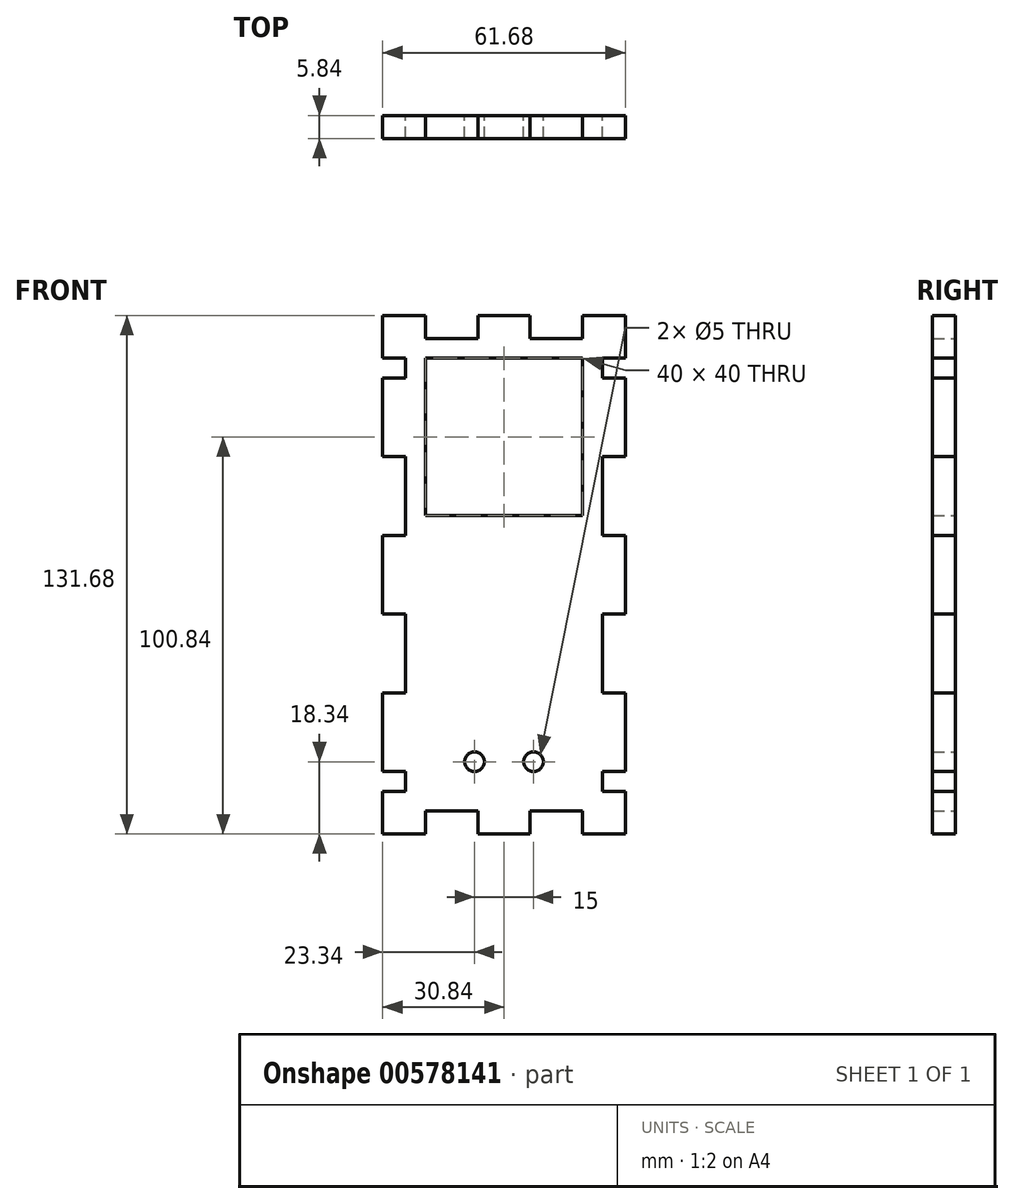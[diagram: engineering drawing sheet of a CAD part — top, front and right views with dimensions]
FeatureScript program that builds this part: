
annotation { "Feature Type Name" : "Feature", "Feature Type Description" : "" }
export const myFeature = defineFeature(function(context is Context, id is Id, definition is map)
    precondition{}
    {
        {
            var Q0;
            Q0=qCreatedBy(makeId("Front.planeOp"),FACE);
            var sketch = newSketch(context, id + "F0", { "sketchPlane" : qUnion([Q0])});
            skLineSegment(sketch, "E0.bottom", {"start": v(-25, 60) * mm, "end": v(25, 60) * mm});
            skLineSegment(sketch, "E0.top", {"start": v(-25, -60) * mm, "end": v(25, -60) * mm});
            skLineSegment(sketch, "E0.left", {"start": v(-25, 60) * mm, "end": v(-25, -60) * mm});
            skLineSegment(sketch, "E0.right", {"start": v(25, 60) * mm, "end": v(25, -60) * mm});
            skLineSegment(sketch, "E1.bottom", {"start": v(30.84, 65.84) * mm, "end": v(20, 65.84) * mm});
            skLineSegment(sketch, "E1.top", {"start": v(30.84, -65.84) * mm, "end": v(20, -65.84) * mm});
            skLineSegment(sketch, "E1.left", {"start": v(30.84, 65.84) * mm, "end": v(30.84, 55) * mm});
            skLineSegment(sketch, "E1.right", {"start": v(-30.84, 65.84) * mm, "end": v(-30.84, 55) * mm});
            skPoint(sketch, "E1.middle", {"position": v(0, 0) * mm});
            skLineSegment(sketch, "E2.bottom", {"start": v(6.67, -65.84) * mm, "end": v(-6.67, -65.84) * mm});
            skLineSegment(sketch, "E2.left", {"start": v(6.67, -65.84) * mm, "end": v(6.67, -60) * mm});
            skLineSegment(sketch, "E2.right", {"start": v(-6.67, -65.84) * mm, "end": v(-6.67, -60) * mm});
            skPoint(sketch, "E2.middle", {"position": v(0, -60) * mm});
            skPoint(sketch, "E3.middle", {"position": v(-25, -60) * mm});
            skLineSegment(sketch, "E4.bottom", {"start": v(-6.67, 65.84) * mm, "end": v(6.67, 65.84) * mm});
            skLineSegment(sketch, "E4.left", {"start": v(-6.67, 65.84) * mm, "end": v(-6.67, 60) * mm});
            skLineSegment(sketch, "E4.right", {"start": v(6.67, 65.84) * mm, "end": v(6.67, 60) * mm});
            skPoint(sketch, "E4.middle", {"position": v(0, 60) * mm});
            skPoint(sketch, "E5.middle", {"position": v(-25, 60) * mm});
            skPoint(sketch, "E6.middle", {"position": v(25, 60) * mm});
            skLineSegment(sketch, "E7.bottom", {"start": v(-6.67, 60) * mm, "end": v(-20, 60) * mm});
            skLineSegment(sketch, "E7.left", {"start": v(-6.67, 60) * mm, "end": v(-6.67, 65.84) * mm});
            skLineSegment(sketch, "E7.right", {"start": v(-20, 60) * mm, "end": v(-20, 65.84) * mm});
            skLineSegment(sketch, "E8.bottom", {"start": v(6.67, 60) * mm, "end": v(20, 60) * mm});
            skLineSegment(sketch, "E8.left", {"start": v(6.67, 60) * mm, "end": v(6.67, 65.84) * mm});
            skLineSegment(sketch, "E8.right", {"start": v(20, 60) * mm, "end": v(20, 65.84) * mm});
            skLineSegment(sketch, "E9.bottom", {"start": v(-6.67, -60) * mm, "end": v(-20, -60) * mm});
            skLineSegment(sketch, "E9.left", {"start": v(-6.67, -60) * mm, "end": v(-6.67, -65.84) * mm});
            skLineSegment(sketch, "E9.right", {"start": v(-20, -60) * mm, "end": v(-20, -65.84) * mm});
            skLineSegment(sketch, "E10.bottom", {"start": v(6.67, -60) * mm, "end": v(20, -60) * mm});
            skLineSegment(sketch, "E10.left", {"start": v(6.67, -60) * mm, "end": v(6.67, -65.84) * mm});
            skLineSegment(sketch, "E10.right", {"start": v(20, -60) * mm, "end": v(20, -65.84) * mm});
            skLineSegment(sketch, "E11.trimOffspring", {"start": v(-20, 65.84) * mm, "end": v(-30.84, 65.84) * mm});
            skLineSegment(sketch, "E12.trimOffspring", {"start": v(6.67, 65.84) * mm, "end": v(-6.67, 65.84) * mm});
            skPoint(sketch, "E13.orphan", {"position": v(-6.67, 54.16) * mm});
            skPoint(sketch, "E14.orphan", {"position": v(6.67, 54.16) * mm});
            skPoint(sketch, "E15.orphan", {"position": v(-6.67, -54.16) * mm});
            skPoint(sketch, "E16.orphan", {"position": v(6.67, -54.16) * mm});
            skLineSegment(sketch, "E17.trimOffspring", {"start": v(-20, -65.84) * mm, "end": v(-30.84, -65.84) * mm});
            skLineSegment(sketch, "E18.bottom", {"start": v(-25, 10) * mm, "end": v(-30.84, 10) * mm});
            skLineSegment(sketch, "E18.top", {"start": v(-25, -10) * mm, "end": v(-30.84, -10) * mm});
            skLineSegment(sketch, "E18.left", {"start": v(-25, 10) * mm, "end": v(-25, -10) * mm});
            skPoint(sketch, "E18.middle", {"position": v(-30.84, 0) * mm});
            skLineSegment(sketch, "E19.bottom", {"start": v(-30.84, 10) * mm, "end": v(-25, 10) * mm});
            skLineSegment(sketch, "E19.top", {"start": v(-30.84, 30) * mm, "end": v(-25, 30) * mm});
            skLineSegment(sketch, "E19.right", {"start": v(-25, 10) * mm, "end": v(-25, 30) * mm});
            skPoint(sketch, "E19.middle", {"position": v(-30.84, 20) * mm});
            skLineSegment(sketch, "E20.bottom", {"start": v(-30.84, -10) * mm, "end": v(-25, -10) * mm});
            skLineSegment(sketch, "E20.top", {"start": v(-30.84, -30) * mm, "end": v(-25, -30) * mm});
            skLineSegment(sketch, "E20.right", {"start": v(-25, -10) * mm, "end": v(-25, -30) * mm});
            skPoint(sketch, "E20.middle", {"position": v(-30.84, -20) * mm});
            skLineSegment(sketch, "E21.top", {"start": v(-30.84, 50) * mm, "end": v(-25, 50) * mm});
            skLineSegment(sketch, "E21.right", {"start": v(-25, 30) * mm, "end": v(-25, 50) * mm});
            skPoint(sketch, "E21.middle", {"position": v(-30.84, 40) * mm});
            skPoint(sketch, "E22.cornerSnap0", {"position": v(-36.68, 20) * mm});
            skLineSegment(sketch, "E23.top", {"start": v(-30.84, -50) * mm, "end": v(-25, -50) * mm});
            skLineSegment(sketch, "E23.right", {"start": v(-25, -30) * mm, "end": v(-25, -50) * mm});
            skPoint(sketch, "E23.middle", {"position": v(-30.84, -40) * mm});
            skLineSegment(sketch, "E24.top", {"start": v(-101.7, -103.63) * mm, "end": v(-97.86, -103.63) * mm});
            skLineSegment(sketch, "E25.bottom", {"start": v(-25, 55) * mm, "end": v(-30.84, 55) * mm});
            skLineSegment(sketch, "E25.top", {"start": v(-25, 50) * mm, "end": v(-30.84, 50) * mm});
            skLineSegment(sketch, "E25.left", {"start": v(-25, 55) * mm, "end": v(-25, 50) * mm});
            skLineSegment(sketch, "E26.bottom", {"start": v(-25, -50) * mm, "end": v(-30.84, -50) * mm});
            skLineSegment(sketch, "E26.top", {"start": v(-25, -55) * mm, "end": v(-30.84, -55) * mm});
            skLineSegment(sketch, "E26.left", {"start": v(-25, -50) * mm, "end": v(-25, -55) * mm});
            skLineSegment(sketch, "E27.bottom", {"start": v(25, 10) * mm, "end": v(30.84, 10) * mm});
            skLineSegment(sketch, "E27.top", {"start": v(25, -10) * mm, "end": v(30.84, -10) * mm});
            skLineSegment(sketch, "E27.left", {"start": v(25, 10) * mm, "end": v(25, -10) * mm});
            skPoint(sketch, "E27.middle", {"position": v(30.84, 0) * mm});
            skLineSegment(sketch, "E28.bottom", {"start": v(30.84, 10) * mm, "end": v(25, 10) * mm});
            skLineSegment(sketch, "E28.top", {"start": v(30.84, 30) * mm, "end": v(25, 30) * mm});
            skLineSegment(sketch, "E28.right", {"start": v(25, 10) * mm, "end": v(25, 30) * mm});
            skPoint(sketch, "E28.middle", {"position": v(30.84, 20) * mm});
            skLineSegment(sketch, "E29.bottom", {"start": v(30.84, -10) * mm, "end": v(25, -10) * mm});
            skLineSegment(sketch, "E29.top", {"start": v(30.84, -30) * mm, "end": v(25, -30) * mm});
            skLineSegment(sketch, "E29.right", {"start": v(25, -10) * mm, "end": v(25, -30) * mm});
            skPoint(sketch, "E29.middle", {"position": v(30.84, -20) * mm});
            skLineSegment(sketch, "E30.top", {"start": v(30.84, 50) * mm, "end": v(25, 50) * mm});
            skLineSegment(sketch, "E30.right", {"start": v(25, 30) * mm, "end": v(25, 50) * mm});
            skPoint(sketch, "E30.middle", {"position": v(30.84, 40) * mm});
            skLineSegment(sketch, "E31.top", {"start": v(30.84, -50) * mm, "end": v(25, -50) * mm});
            skLineSegment(sketch, "E31.right", {"start": v(25, -30) * mm, "end": v(25, -50) * mm});
            skPoint(sketch, "E31.middle", {"position": v(30.84, -40) * mm});
            skLineSegment(sketch, "E32.bottom", {"start": v(25, -50) * mm, "end": v(30.84, -50) * mm});
            skLineSegment(sketch, "E32.top", {"start": v(25, -55) * mm, "end": v(30.84, -55) * mm});
            skLineSegment(sketch, "E32.left", {"start": v(25, -50) * mm, "end": v(25, -55) * mm});
            skLineSegment(sketch, "E33.bottom", {"start": v(25, 55) * mm, "end": v(30.84, 55) * mm});
            skLineSegment(sketch, "E33.top", {"start": v(25, 50) * mm, "end": v(30.84, 50) * mm});
            skLineSegment(sketch, "E33.left", {"start": v(25, 55) * mm, "end": v(25, 50) * mm});
            skPoint(sketch, "E34.orphan", {"position": v(-36.68, 50) * mm});
            skPoint(sketch, "E35.orphan", {"position": v(-36.68, 30) * mm});
            skPoint(sketch, "E36.orphan", {"position": v(-36.68, 10) * mm});
            skPoint(sketch, "E37.orphan", {"position": v(-36.68, -10) * mm});
            skPoint(sketch, "E38.orphan", {"position": v(-36.68, -30) * mm});
            skPoint(sketch, "E26.right.end.orphan", {"position": v(-36.68, -55) * mm});
            skPoint(sketch, "E39.orphan", {"position": v(-36.68, -50) * mm});
            skPoint(sketch, "E40.orphan", {"position": v(36.68, 10) * mm});
            skPoint(sketch, "E41.orphan", {"position": v(36.68, -10) * mm});
            skPoint(sketch, "E42.orphan", {"position": v(36.68, -30) * mm});
            skPoint(sketch, "E43.orphan", {"position": v(36.68, -50) * mm});
            skPoint(sketch, "E44.orphan", {"position": v(36.68, -55) * mm});
            skPoint(sketch, "E45.orphan", {"position": v(36.68, 50) * mm});
            skPoint(sketch, "E46.orphan", {"position": v(36.68, 30) * mm});
            skLineSegment(sketch, "E47.bottom", {"start": v(-20, 60) * mm, "end": v(-6.67, 60) * mm});
            skLineSegment(sketch, "E48.trimOffspring", {"start": v(-30.84, 50) * mm, "end": v(-30.84, 30) * mm});
            skLineSegment(sketch, "E49.trimOffspring", {"start": v(30.84, 50) * mm, "end": v(30.84, 30) * mm});
            skLineSegment(sketch, "E50.trimOffspring", {"start": v(30.84, 10) * mm, "end": v(30.84, -10) * mm});
            skLineSegment(sketch, "E51.trimOffspring", {"start": v(30.84, -30) * mm, "end": v(30.84, -50) * mm});
            skLineSegment(sketch, "E52.trimOffspring", {"start": v(30.84, -55) * mm, "end": v(30.84, -65.84) * mm});
            skLineSegment(sketch, "E53.trimOffspring", {"start": v(-30.84, -55) * mm, "end": v(-30.84, -65.84) * mm});
            skLineSegment(sketch, "E54.trimOffspring", {"start": v(-30.84, -20) * mm, "end": v(-30.84, -50) * mm});
            skLineSegment(sketch, "E55.trimOffspring", {"start": v(-30.84, 10) * mm, "end": v(-30.84, -10) * mm});
            skCircle(sketch, "E56", {"center": v(7.5, -47.5) * mm, "radius": 2.5 * mm});
            skCircle(sketch, "E57", {"center": v(-7.5, -47.5) * mm, "radius": 2.5 * mm});
            skLineSegment(sketch, "E58.bottom", {"start": v(20, 55) * mm, "end": v(-20, 55) * mm});
            skLineSegment(sketch, "E58.top", {"start": v(20, 15) * mm, "end": v(-20, 15) * mm});
            skLineSegment(sketch, "E58.left", {"start": v(20, 55) * mm, "end": v(20, 15) * mm});
            skLineSegment(sketch, "E58.right", {"start": v(-20, 55) * mm, "end": v(-20, 15) * mm});
            skPoint(sketch, "E58.middle", {"position": v(0, 35) * mm});
            skSolve(sketch);
        }
        {
            var Q0;
            Q0=qSketchRegion(id+"F0",true);
            extrude(context, id + "F1", {"entities" : qUnion([Q0]), "depth" : 5.84 * mm, "offsetDistance" : 25 * mm});
        }
    });
